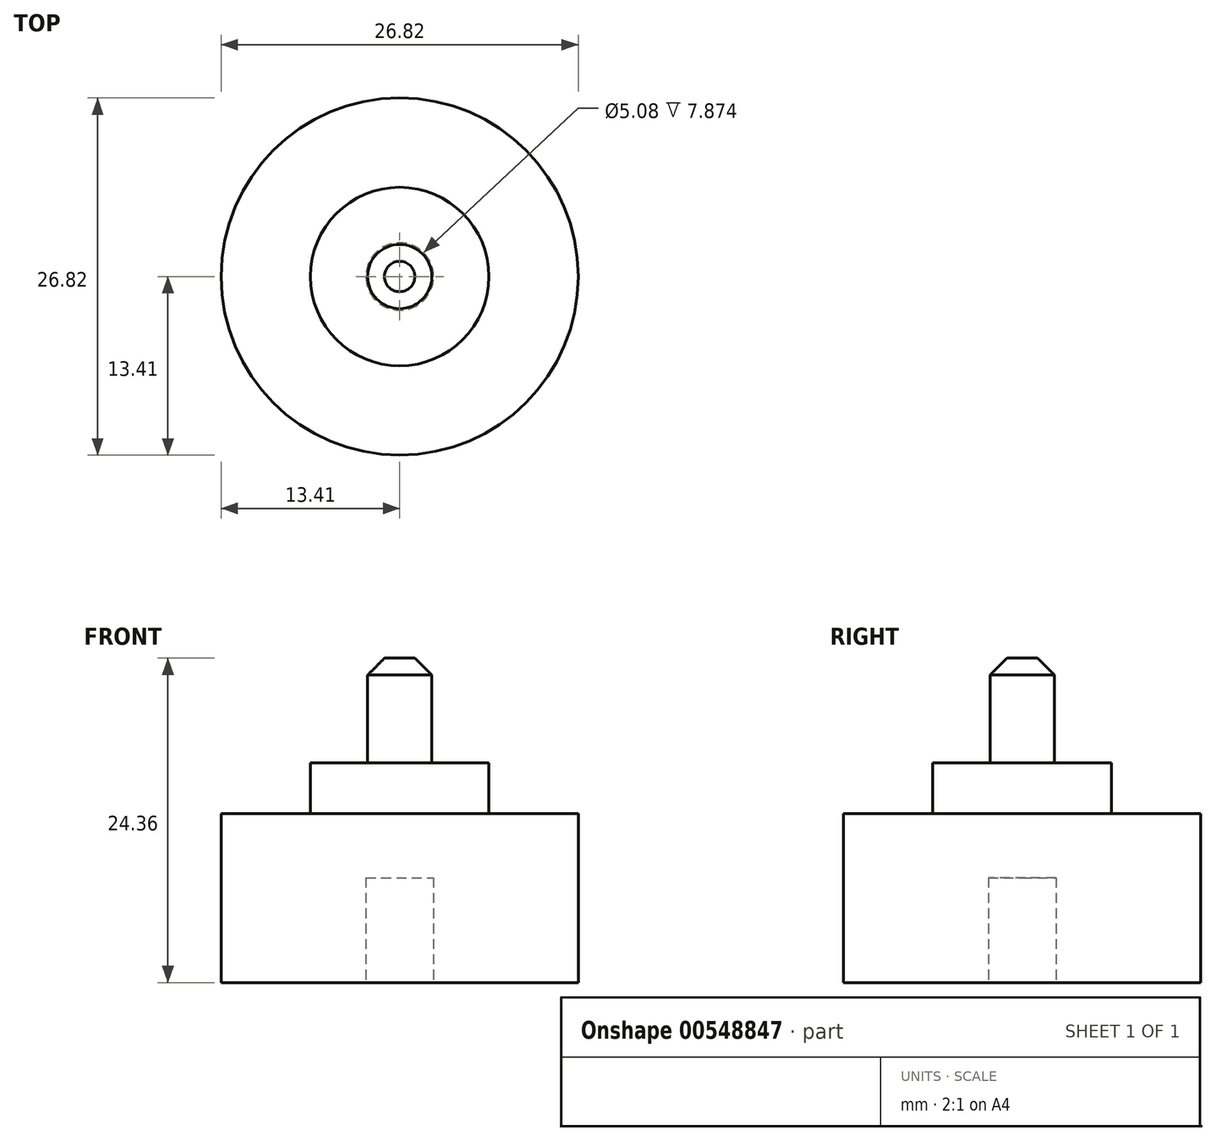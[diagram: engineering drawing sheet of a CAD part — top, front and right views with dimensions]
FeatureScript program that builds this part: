
annotation { "Feature Type Name" : "Feature", "Feature Type Description" : "" }
export const myFeature = defineFeature(function(context is Context, id is Id, definition is map)
    precondition{}
    {
        {
            var Q0;
            Q0=qCreatedBy(makeId("Front.planeOp"),FACE);
            var sketch = newSketch(context, id + "F0", { "sketchPlane" : qUnion([Q0])});
            skLineSegment(sketch, "E0", {"start": v(0, 0) * mm, "end": v(13.41, 0) * mm});
            skLineSegment(sketch, "E1", {"start": v(13.41, 0) * mm, "end": v(13.41, 12.7) * mm});
            skLineSegment(sketch, "E2", {"start": v(13.41, 12.7) * mm, "end": v(6.7, 12.7) * mm});
            skLineSegment(sketch, "E3", {"start": v(2.41, 16.51) * mm, "end": v(6.7, 16.51) * mm});
            skPoint(sketch, "E3.endSnap0", {"position": v(6.7, 12.7) * mm});
            skLineSegment(sketch, "E4", {"start": v(6.7, 16.51) * mm, "end": v(6.7, 12.7) * mm});
            skLineSegment(sketch, "E5", {"start": v(0, 24.36) * mm, "end": v(2.41, 24.36) * mm});
            skLineSegment(sketch, "E6", {"start": v(2.41, 24.36) * mm, "end": v(2.41, 16.51) * mm});
            skPoint(sketch, "E7.start.orphan", {"position": v(0, 12.7) * mm});
            skLineSegment(sketch, "E8", {"start": v(0, 0) * mm, "end": v(2.54, 0) * mm});
            skLineSegment(sketch, "E9", {"start": v(2.54, 0) * mm, "end": v(2.54, 7.87) * mm});
            skLineSegment(sketch, "E10", {"start": v(2.54, 7.87) * mm, "end": v(0, 7.87) * mm});
            skLineSegment(sketch, "E11", {"start": v(0, 7.87) * mm, "end": v(0, 24.36) * mm});
            skSolve(sketch);
        }
        {
            var Q0;
            Q0 = qSketchRegion(id + "F0", true);
            var Q1;
            Q1=sQuery(id+"F0.wireOp",EDGE,"E11");
            revolve(context, id + "F1", {"entities" : qUnion([Q0]), "axis" : qUnion([Q1]), "revolveType" : RevolveType.FULL});
        }
        {
            var Q0;
            Q0=makeQuery(id+"F1.opRevolve","SWEPT_EDGE",EDGE,{"disambiguationData":[OSD([sQuery(id+"F0.wireOp",EDGE,"E5"),sQuery(id+"F0.wireOp",EDGE,"E6")])]});
            chamfer(context, id + "F2", {"entities" : qUnion([Q0]), "width" : 1.27 * mm, "tangentPropagation" : true});
        }
    });
